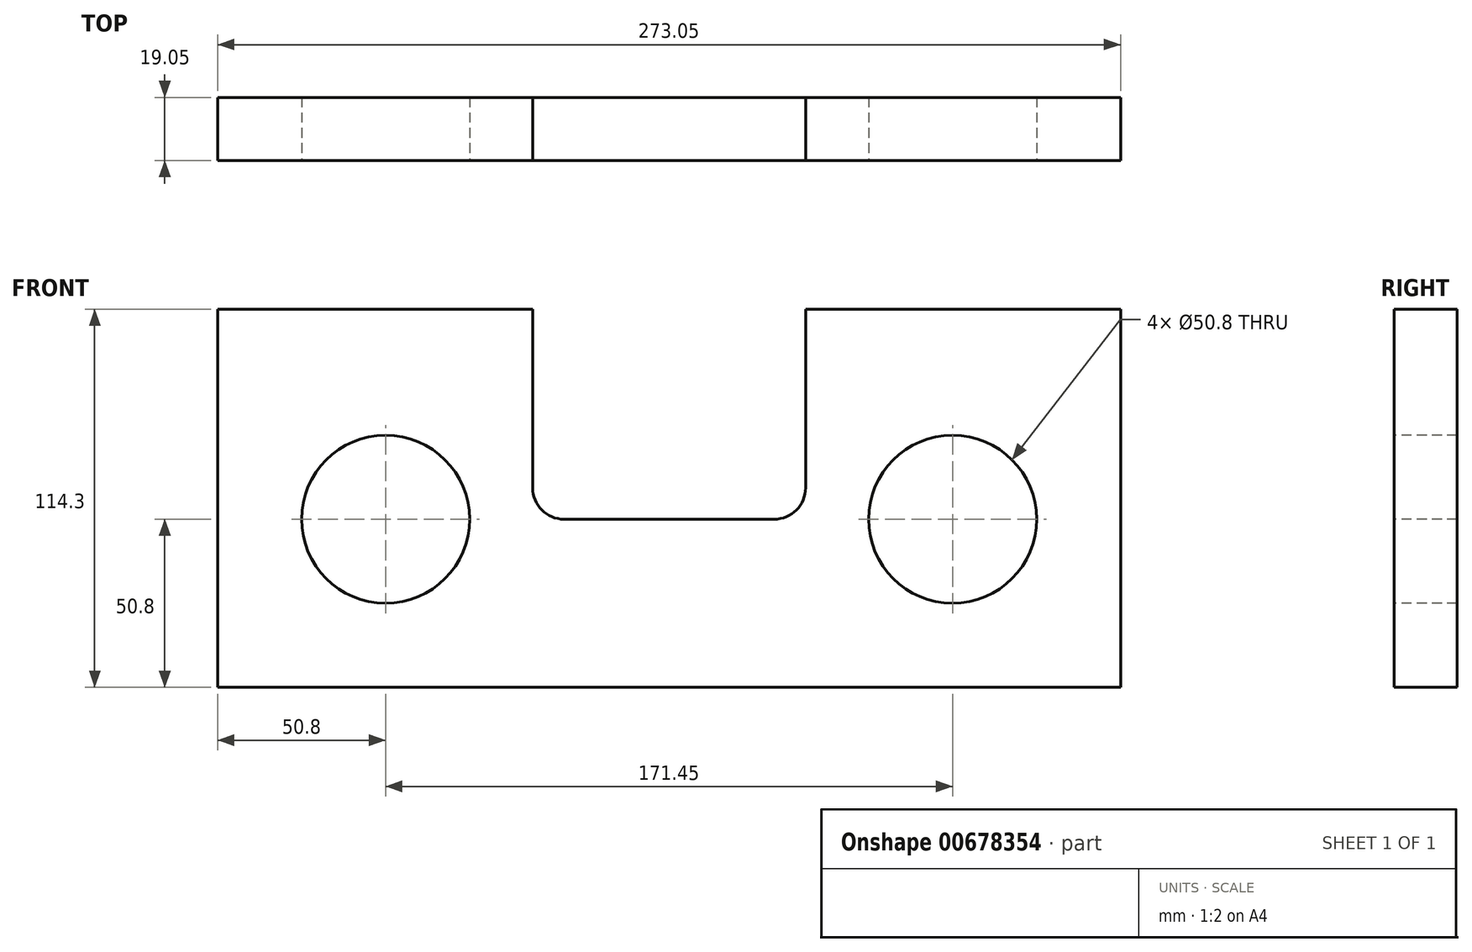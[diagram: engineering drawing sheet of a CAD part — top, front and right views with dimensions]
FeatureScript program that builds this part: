
annotation { "Feature Type Name" : "Feature", "Feature Type Description" : "" }
export const myFeature = defineFeature(function(context is Context, id is Id, definition is map)
    precondition{}
    {
        {
            var Q0;
            Q0=qCreatedBy(makeId("Front.planeOp"),FACE);
            var sketch = newSketch(context, id + "F0", { "sketchPlane" : qUnion([Q0])});
            skLineSegment(sketch, "E0.bottom", {"start": v(0, 0) * mm, "end": v(273.05, 0) * mm});
            skLineSegment(sketch, "E0.top", {"start": v(0, 114.3) * mm, "end": v(273.05, 114.3) * mm});
            skLineSegment(sketch, "E0.left", {"start": v(0, 0) * mm, "end": v(0, 114.3) * mm});
            skLineSegment(sketch, "E0.right", {"start": v(273.05, 0) * mm, "end": v(273.05, 114.3) * mm});
            skSolve(sketch);
        }
        {
            var Q0;
            Q0=makeQuery(id+"F0.imprint","IMPRINT",FACE,{"disambiguationData":[TD([[makeQuery(id+"F0.imprint","IMPRINT",EDGE,{"derivedFrom":sQuery(id+"F0.wireOp",EDGE,"E0.bottom")}),1.0]])]});
            extrude(context, id + "F1", {"entities" : qUnion([Q0]), "depth" : 19.05 * mm, "offsetDistance" : 25.4 * mm});
        }
        {
            var Q0;
            Q0=makeQuery(id+"F1.opExtrude","CAP_FACE",FACE,{"disambiguationData":[OSD([sQuery(id+"F0.wireOp",EDGE,"E0.bottom"),sQuery(id+"F0.wireOp",EDGE,"E0.top"),sQuery(id+"F0.wireOp",EDGE,"E0.left"),sQuery(id+"F0.wireOp",EDGE,"E0.right")])],"isStart":false});
            var sketch = newSketch(context, id + "F2", { "sketchPlane" : qUnion([Q0])});
            skCircle(sketch, "E1", {"center": v(50.8, 50.8) * mm, "radius": 25.4 * mm});
            skCircle(sketch, "E2", {"center": v(222.25, 50.8) * mm, "radius": 25.4 * mm});
            skSolve(sketch);
        }
        {
            var Q0;
            Q0 = qSketchRegion(id + "F2", true);
            extrude(context, id + "F3", {"entities" : qUnion([Q0]), "operationType" : NewBodyOperationType.REMOVE, "oppositeDirection" : true, "depth" : 25.4 * mm, "offsetDistance" : 25.4 * mm});
        }
        {
            var Q0;
            Q0=makeQuery(id+"F1.opExtrude","CAP_FACE",FACE,{"disambiguationData":[OSD([sQuery(id+"F0.wireOp",EDGE,"E0.bottom"),sQuery(id+"F0.wireOp",EDGE,"E0.top"),sQuery(id+"F0.wireOp",EDGE,"E0.left"),sQuery(id+"F0.wireOp",EDGE,"E0.right")])],"isStart":false});
            var sketch = newSketch(context, id + "F4", { "sketchPlane" : qUnion([Q0])});
            skLineSegment(sketch, "E3", {"start": v(95.25, 114.3) * mm, "end": v(95.25, 60.32) * mm});
            skLineSegment(sketch, "E4", {"start": v(104.78, 50.8) * mm, "end": v(168.28, 50.8) * mm});
            skLineSegment(sketch, "E5", {"start": v(177.8, 60.32) * mm, "end": v(177.8, 114.3) * mm});
            skArc(sketch, "E6", {"start": v(95.25, 60.32) * mm, "mid": v(98.04, 53.59) * mm, "end": v(104.78, 50.8) * mm});
            skArc(sketch, "E7", {"start": v(168.28, 50.8) * mm, "mid": v(175.01, 53.59) * mm, "end": v(177.8, 60.32) * mm});
            skLineSegment(sketch, "E8", {"start": v(95.25, 114.3) * mm, "end": v(177.8, 114.3) * mm});
            skSolve(sketch);
        }
        {
            var Q0;
            Q0=makeQuery(id+"F4.imprint","IMPRINT",FACE,{"disambiguationData":[TD([[makeQuery(id+"F4.imprint","IMPRINT",EDGE,{"derivedFrom":sQuery(id+"F4.wireOp",EDGE,"E3")}),1.0]])]});
            extrude(context, id + "F5", {"entities" : qUnion([Q0]), "operationType" : NewBodyOperationType.REMOVE, "oppositeDirection" : true, "depth" : 25.4 * mm, "offsetDistance" : 25.4 * mm});
        }
    });
